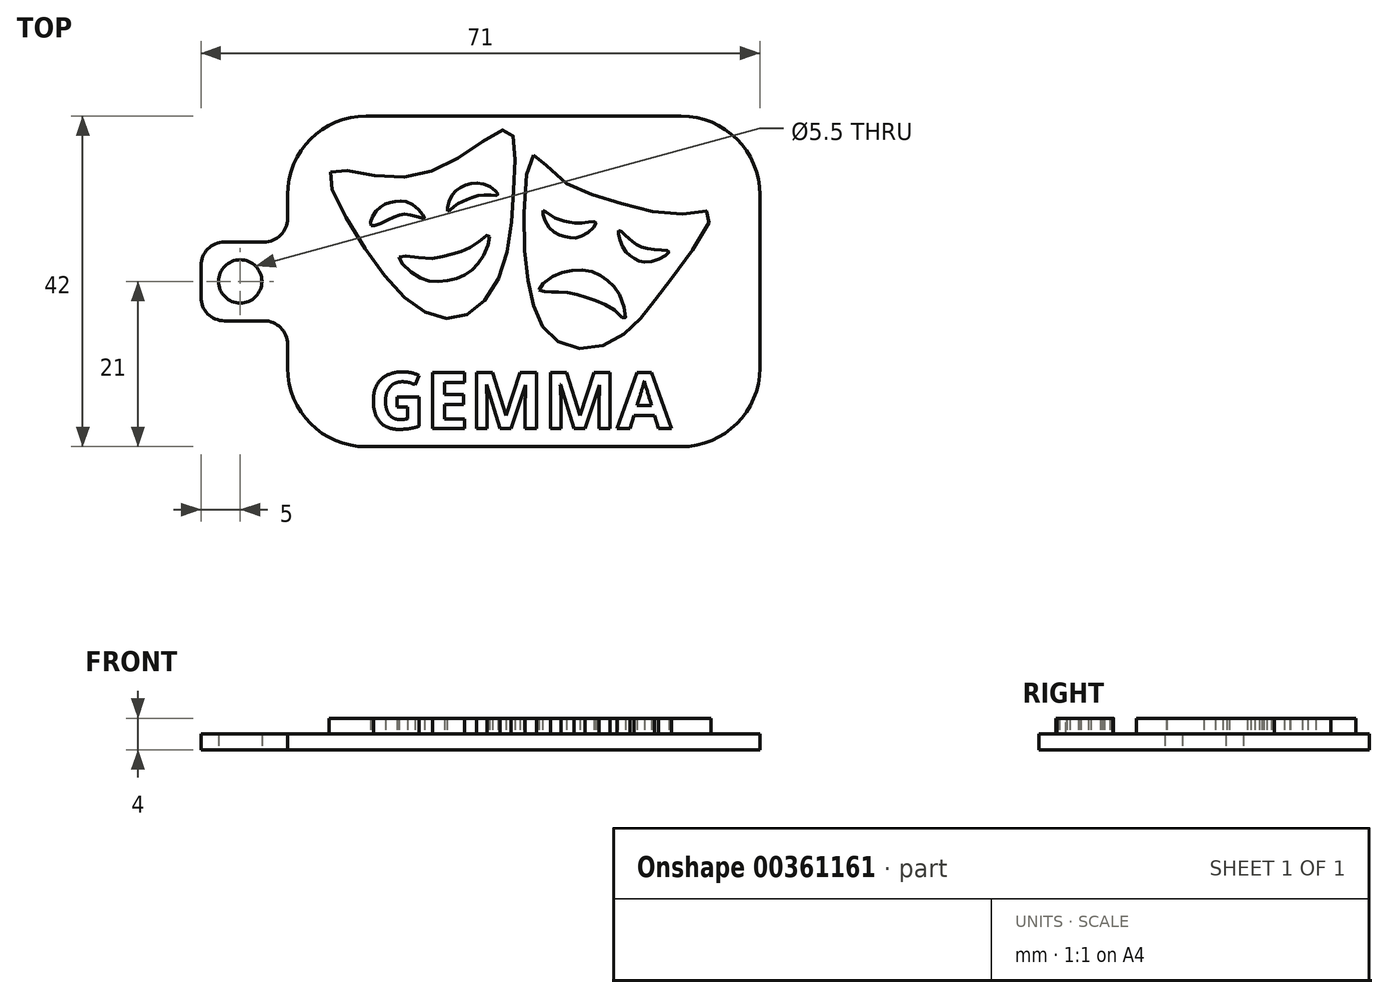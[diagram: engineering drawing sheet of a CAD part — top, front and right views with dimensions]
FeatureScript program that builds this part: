
annotation { "Feature Type Name" : "Feature", "Feature Type Description" : "" }
export const myFeature = defineFeature(function(context is Context, id is Id, definition is map)
    precondition{}
    {
        {
            var Q0;
            Q0=qCreatedBy(makeId("Top.planeOp"),FACE);
            var sketch = newSketch(context, id + "F0", { "sketchPlane" : qUnion([Q0])});
            skLineSegment(sketch, "E0.bottom", {"start": v(20, 21) * mm, "end": v(-20, 21) * mm});
            skLineSegment(sketch, "E0.top", {"start": v(20, -21) * mm, "end": v(-20, -21) * mm});
            skLineSegment(sketch, "E0.left", {"start": v(30, 11) * mm, "end": v(30, -11) * mm});
            skLineSegment(sketch, "E0.right", {"start": v(-30, 11) * mm, "end": v(-30, 8) * mm});
            skLineSegment(sketch, "E1.bottom", {"start": v(-38, 5) * mm, "end": v(-33, 5) * mm});
            skLineSegment(sketch, "E1.top", {"start": v(-38, -5) * mm, "end": v(-33, -5) * mm});
            skLineSegment(sketch, "E1.left", {"start": v(-41, 2) * mm, "end": v(-41, -2) * mm});
            skLineSegment(sketch, "E2.trimOffspring", {"start": v(-30, -8) * mm, "end": v(-30, -11) * mm});
            skPoint(sketch, "E3.visualSharp", {"position": v(-30, 5) * mm});
            skArc(sketch, "E3.filletArc", {"start": v(-33, 5) * mm, "mid": v(-30.88, 5.88) * mm, "end": v(-30, 8) * mm});
            skPoint(sketch, "E4.visualSharp", {"position": v(-41, 5) * mm});
            skArc(sketch, "E4.filletArc", {"start": v(-38, 5) * mm, "mid": v(-40.12, 4.12) * mm, "end": v(-41, 2) * mm});
            skPoint(sketch, "E5.visualSharp", {"position": v(-41, -5) * mm});
            skArc(sketch, "E5.filletArc", {"start": v(-41, -2) * mm, "mid": v(-40.12, -4.12) * mm, "end": v(-38, -5) * mm});
            skPoint(sketch, "E6.visualSharp", {"position": v(-30, -5) * mm});
            skArc(sketch, "E6.filletArc", {"start": v(-30, -8) * mm, "mid": v(-30.88, -5.88) * mm, "end": v(-33, -5) * mm});
            skPoint(sketch, "E7.visualSharp", {"position": v(-30, 21) * mm});
            skArc(sketch, "E7.filletArc", {"start": v(-20, 21) * mm, "mid": v(-27.07, 18.07) * mm, "end": v(-30, 11) * mm});
            skPoint(sketch, "E8.visualSharp", {"position": v(-30, -21) * mm});
            skArc(sketch, "E8.filletArc", {"start": v(-30, -11) * mm, "mid": v(-27.07, -18.07) * mm, "end": v(-20, -21) * mm});
            skPoint(sketch, "E9.visualSharp", {"position": v(30, 21) * mm});
            skArc(sketch, "E9.filletArc", {"start": v(30, 11) * mm, "mid": v(27.07, 18.07) * mm, "end": v(20, 21) * mm});
            skPoint(sketch, "E10.visualSharp", {"position": v(30, -21) * mm});
            skArc(sketch, "E10.filletArc", {"start": v(20, -21) * mm, "mid": v(27.07, -18.07) * mm, "end": v(30, -11) * mm});
            skCircle(sketch, "E11", {"center": v(-36, 0) * mm, "radius": 2.75 * mm});
            skPoint(sketch, "E11.centerSnap0", {"position": v(-41, 0) * mm});
            skSolve(sketch);
        }
        {
            var Q0;
            Q0=makeQuery(id+"F0.imprint","IMPRINT",FACE,{"disambiguationData":[TD([[makeQuery(id+"F0.imprint","IMPRINT",EDGE,{"derivedFrom":sQuery(id+"F0.wireOp",EDGE,"E0.bottom")}),1.0]])]});
            extrude(context, id + "F1", {"entities" : qUnion([Q0]), "depth" : 2 * mm});
        }
        {
            var Q0;
            {var subQ0=sQuery(id+"F0.wireOp",EDGE,"E11");var subQ1=sQuery(id+"F0.wireOp",EDGE,"E10.filletArc");var subQ2=sQuery(id+"F0.wireOp",EDGE,"E9.filletArc");var subQ3=sQuery(id+"F0.wireOp",EDGE,"E8.filletArc");var subQ4=sQuery(id+"F0.wireOp",EDGE,"E7.filletArc");var subQ5=sQuery(id+"F0.wireOp",EDGE,"E6.filletArc");var subQ6=sQuery(id+"F0.wireOp",EDGE,"E5.filletArc");var subQ7=sQuery(id+"F0.wireOp",EDGE,"E0.left");var subQ8=sQuery(id+"F0.wireOp",EDGE,"E0.top");var subQ9=sQuery(id+"F0.wireOp",EDGE,"E0.right");var subQ10=sQuery(id+"F0.wireOp",EDGE,"E0.bottom");var subQ11=sQuery(id+"F0.wireOp",EDGE,"E4.filletArc");var subQ12=sQuery(id+"F0.wireOp",EDGE,"E1.bottom");var subQ13=sQuery(id+"F0.wireOp",EDGE,"E1.top");var subQ14=sQuery(id+"F0.wireOp",EDGE,"E1.left");var subQ15=sQuery(id+"F0.wireOp",EDGE,"E2.trimOffspring");var subQ16=sQuery(id+"F0.wireOp",EDGE,"E3.filletArc");Q0=makeQuery(id+"FYQyjegr8MfedOk_1.boolean.opBoolean","SPLIT",FACE,{"disambiguationData":[TD([makeQuery(id+"F1.opExtrude","SWEPT_FACE",FACE,{"disambiguationData":[OSD([subQ10])]})])],"derivedFrom":makeQuery(id+"F1.opExtrude","CAP_FACE",FACE,{"disambiguationData":[OSD([subQ10,subQ8,subQ7,subQ9,subQ12,subQ13,subQ14,subQ15,subQ16,subQ11,subQ6,subQ5,subQ4,subQ3,subQ2,subQ1,subQ0])],"isStart":false})});}
            var sketch = newSketch(context, id + "F2", { "sketchPlane" : qUnion([Q0])});
            skText(sketch, "E12", { "text": "GEMMA", "fontName": "OpenSans-Bold.ttf"});
            skPoint(sketch, "E12.secondSnap0", {"position": v(-18.02, -3.42) * mm});
            const initialGuessF2  = {"E12": [-0.01968, -0.0187, 1, 0, 0.00717]};
            skSetInitialGuess(sketch, initialGuessF2);
            skSolve(sketch);
        }
        {
            var Q0;
            Q0=qSketchRegion(id+"F2",true);
            extrude(context, id + "F3", {"entities" : qUnion([Q0]), "operationType" : NewBodyOperationType.ADD, "depth" : 2 * mm});
        }
        {
            var Q0;
            Q0=makeQuery(id+"F1.opExtrude","CAP_FACE",FACE,{"disambiguationData":[OSD([sQuery(id+"F0.wireOp",EDGE,"E0.bottom"),sQuery(id+"F0.wireOp",EDGE,"E0.top"),sQuery(id+"F0.wireOp",EDGE,"E0.left"),sQuery(id+"F0.wireOp",EDGE,"E0.right"),sQuery(id+"F0.wireOp",EDGE,"E1.bottom"),sQuery(id+"F0.wireOp",EDGE,"E1.top"),sQuery(id+"F0.wireOp",EDGE,"E1.left"),sQuery(id+"F0.wireOp",EDGE,"E2.trimOffspring"),sQuery(id+"F0.wireOp",EDGE,"E3.filletArc"),sQuery(id+"F0.wireOp",EDGE,"E4.filletArc"),sQuery(id+"F0.wireOp",EDGE,"E5.filletArc"),sQuery(id+"F0.wireOp",EDGE,"E6.filletArc"),sQuery(id+"F0.wireOp",EDGE,"E7.filletArc"),sQuery(id+"F0.wireOp",EDGE,"E8.filletArc"),sQuery(id+"F0.wireOp",EDGE,"E9.filletArc"),sQuery(id+"F0.wireOp",EDGE,"E10.filletArc"),sQuery(id+"F0.wireOp",EDGE,"E11")])],"isStart":false});
            var sketch = newSketch(context, id + "F4", { "sketchPlane" : qUnion([Q0])});
            skFitSpline(sketch, "E13", {"points": [v(-24.5, 13.9) * mm, v(-20.9, 5.33) * mm, v(-13.22, -3.5) * mm, v(-7.57, -4.38) * mm, v(-2.9, 1.09) * mm, v(-1.21, 12.48) * mm, v(-1.92, 19.24) * mm, v(-7.92, 15.92) * mm, v(-17.81, 13.27) * mm, v(-24.5, 13.9) * mm]});
            skFitSpline(sketch, "E14", {"points": [v(1.27, 16.08) * mm, v(0, 7.12) * mm, v(0.92, -1.83) * mm, v(2.9, -6.38) * mm, v(6.89, -8.52) * mm, v(12, -7.24) * mm, v(15.56, -3.82) * mm, v(19.83, 1.72) * mm, v(23.76, 8.69) * mm, v(19.83, 8.55) * mm, v(10.87, 10.4) * mm, v(4.04, 13.45) * mm, v(1.27, 16.08) * mm]});
            skFitSpline(sketch, "E15", {"points": [v(-19.39, 7.12) * mm, v(-18.68, 9.02) * mm, v(-16.79, 10.06) * mm, v(-14.49, 9.94) * mm, v(-12.63, 8.05) * mm, v(-14.41, 8.46) * mm, v(-16.79, 8.05) * mm, v(-19.39, 7.12) * mm]});
            skFitSpline(sketch, "E16", {"points": [v(-9.66, 8.94) * mm, v(-9.07, 11) * mm, v(-7.4, 12.2) * mm, v(-4.87, 12.32) * mm, v(-3.28, 11) * mm, v(-4.91, 11) * mm, v(-7.29, 10.35) * mm, v(-8.7, 9.65) * mm, v(-9.66, 8.94) * mm]});
            skFitSpline(sketch, "E17", {"points": [v(-15.82, 3.08) * mm, v(-12.3, 2.93) * mm, v(-8.92, 3.52) * mm, v(-6.25, 4.64) * mm, v(-4.43, 5.94) * mm, v(-4.87, 3.7) * mm, v(-6.54, 1.48) * mm, v(-8.59, 0.33) * mm, v(-11.26, 0) * mm, v(-13.82, 0.85) * mm, v(-15.82, 3.08) * mm]});
            skFitSpline(sketch, "E18", {"points": [v(2.46, 8.97) * mm, v(3.3, 6.76) * mm, v(5.38, 5.65) * mm, v(7.45, 5.8) * mm, v(9.18, 7.48) * mm, v(7.28, 7.38) * mm, v(5.04, 7.7) * mm, v(3.6, 8.25) * mm, v(2.46, 8.97) * mm]});
            skFitSpline(sketch, "E19", {"points": [v(12.07, 6.47) * mm, v(12.55, 4.45) * mm, v(14, 2.96) * mm, v(16.11, 2.47) * mm, v(18.45, 3.77) * mm, v(16.52, 4.04) * mm, v(14.2, 4.79) * mm, v(12.96, 5.84) * mm, v(12.07, 6.47) * mm]});
            skFitSpline(sketch, "E20", {"points": [v(1.96, -1.06) * mm, v(3.6, 0.57) * mm, v(6.3, 1.42) * mm, v(8.91, 1.18) * mm, v(10.77, 0) * mm, v(12.19, -1.76) * mm, v(12.89, -4.75) * mm, v(11.37, -3.55) * mm, v(8.78, -2.33) * mm, v(6.34, -1.53) * mm, v(4.18, -1.34) * mm, v(2.92, -1.32) * mm, v(1.96, -1.06) * mm]});
            skSolve(sketch);
        }
        {
            var Q0;
            Q0=makeQuery(id+"F4.imprint","IMPRINT",FACE,{"disambiguationData":[TD([[makeQuery(id+"F4.imprint","IMPRINT",EDGE,{"derivedFrom":sQuery(id+"F4.wireOp",EDGE,"E13")}),1.0]])]});
            var Q1;
            Q1=makeQuery(id+"F4.imprint","IMPRINT",FACE,{"disambiguationData":[TD([[makeQuery(id+"F4.imprint","IMPRINT",EDGE,{"derivedFrom":sQuery(id+"F4.wireOp",EDGE,"E14")}),1.0]])]});
            extrude(context, id + "F5", {"entities" : qUnion([Q0, Q1]), "operationType" : NewBodyOperationType.ADD, "depth" : 2 * mm});
        }
    });
